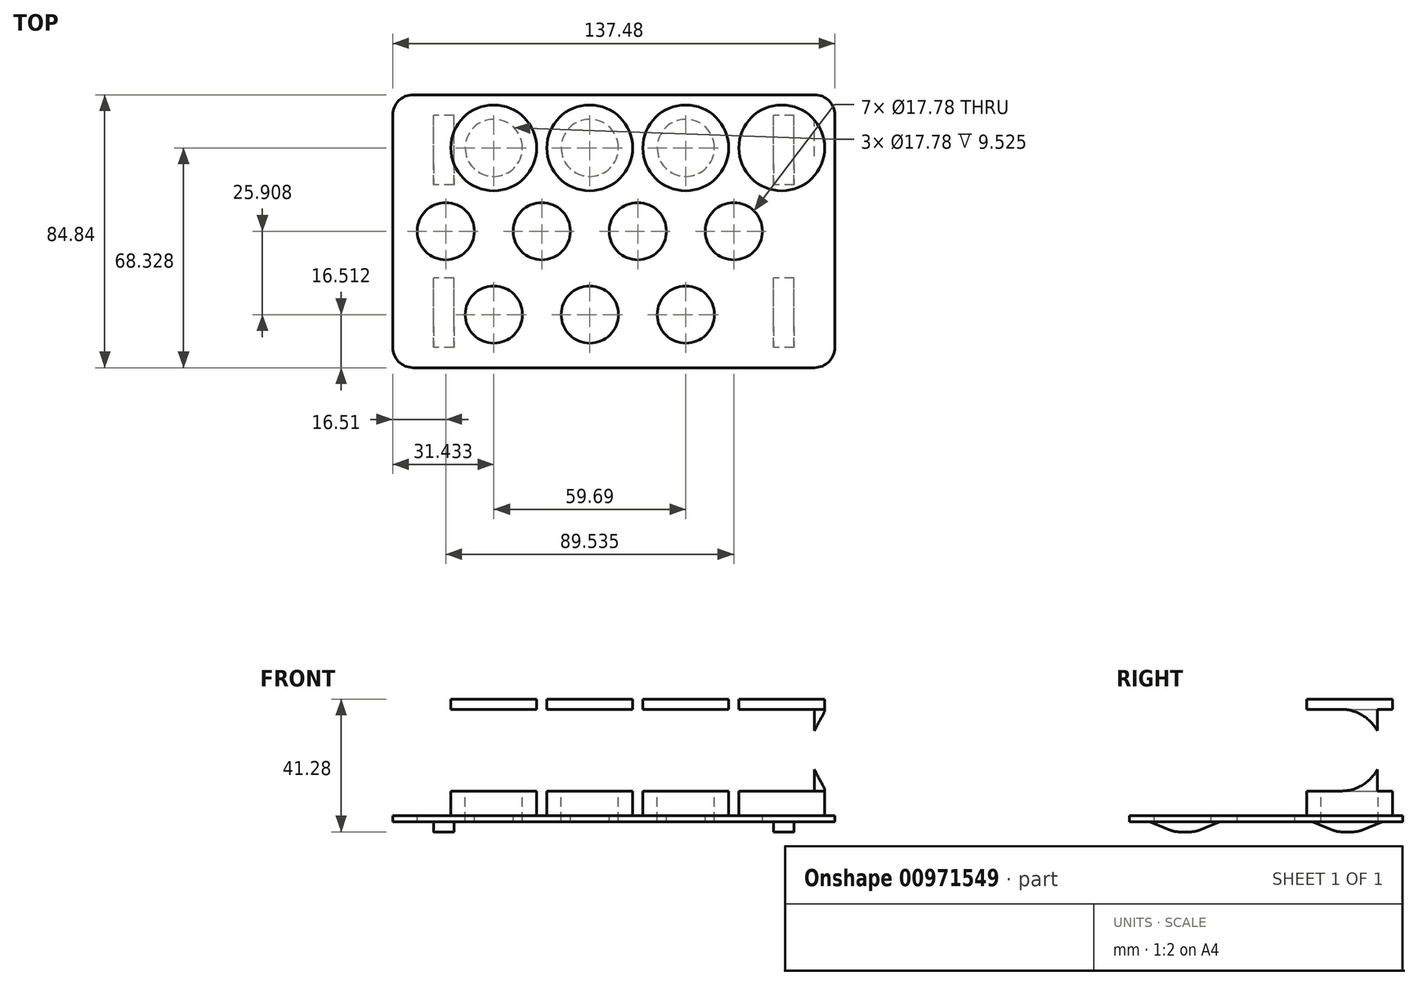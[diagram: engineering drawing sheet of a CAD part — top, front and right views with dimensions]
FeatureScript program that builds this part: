
annotation { "Feature Type Name" : "Feature", "Feature Type Description" : "" }
export const myFeature = defineFeature(function(context is Context, id is Id, definition is map)
    precondition{}
    {
        {
            var Q0;
            Q0=qCreatedBy(makeId("Right.planeOp"),FACE);
            var sketch = newSketch(context, id + "F0", { "sketchPlane" : qUnion([Q0])});
            skLineSegment(sketch, "E0.left", {"start": v(42.42, 20.64) * mm, "end": v(42.42, -17.46) * mm});
            skLineSegment(sketch, "E0.right", {"start": v(-42.42, 20.64) * mm, "end": v(-42.42, -17.46) * mm});
            skLineSegment(sketch, "E1", {"start": v(-42.42, 20.64) * mm, "end": v(42.42, 20.64) * mm});
            skLineSegment(sketch, "E2", {"start": v(28.45, -20.64) * mm, "end": v(22.1, -20.64) * mm});
            skLineSegment(sketch, "E3.top", {"start": v(42.42, -17.46) * mm, "end": v(36.07, -17.46) * mm});
            skLineSegment(sketch, "E4.top", {"start": v(-42.42, -17.46) * mm, "end": v(-36.07, -17.46) * mm});
            skLineSegment(sketch, "E5.top", {"start": v(14.48, -17.46) * mm, "end": v(-14.48, -17.46) * mm});
            skLineSegment(sketch, "E6.trimOffspring", {"start": v(-22.1, -20.64) * mm, "end": v(-28.45, -20.64) * mm});
            skLineSegment(sketch, "E7.bottom", {"start": v(23.37, 17.46) * mm, "end": v(-23.37, 17.46) * mm});
            skLineSegment(sketch, "E7.top", {"start": v(23.37, -7.94) * mm, "end": v(-23.37, -7.94) * mm});
            skLineSegment(sketch, "E7.left", {"start": v(36.07, 4.76) * mm, "end": v(36.07, 4.76) * mm});
            skLineSegment(sketch, "E7.right", {"start": v(-36.07, 4.76) * mm, "end": v(-36.07, 4.76) * mm});
            skPoint(sketch, "E8.visualSharp", {"position": v(36.07, 17.46) * mm});
            skArc(sketch, "E8.filletArc", {"start": v(36.07, 4.76) * mm, "mid": v(32.35, 13.74) * mm, "end": v(23.37, 17.46) * mm});
            skPoint(sketch, "E9.visualSharp", {"position": v(36.07, -7.94) * mm});
            skArc(sketch, "E9.filletArc", {"start": v(23.37, -7.94) * mm, "mid": v(32.35, -4.22) * mm, "end": v(36.07, 4.76) * mm});
            skPoint(sketch, "E10.visualSharp", {"position": v(-36.07, 17.46) * mm});
            skArc(sketch, "E10.filletArc", {"start": v(-23.37, 17.46) * mm, "mid": v(-32.35, 13.74) * mm, "end": v(-36.07, 4.76) * mm});
            skPoint(sketch, "E11.visualSharp", {"position": v(-36.07, -7.94) * mm});
            skArc(sketch, "E11.filletArc", {"start": v(-36.07, 4.76) * mm, "mid": v(-32.35, -4.22) * mm, "end": v(-23.37, -7.94) * mm});
            skLineSegment(sketch, "E12", {"start": v(-28.45, -20.64) * mm, "end": v(-36.07, -17.46) * mm});
            skLineSegment(sketch, "E13", {"start": v(-22.1, -20.64) * mm, "end": v(-14.48, -17.46) * mm});
            skLineSegment(sketch, "E14", {"start": v(22.1, -20.64) * mm, "end": v(14.48, -17.46) * mm});
            skLineSegment(sketch, "E15", {"start": v(28.45, -20.64) * mm, "end": v(36.07, -17.46) * mm});
            skSolve(sketch);
        }
        {
            var Q0;
            {var subQ0=sQuery(id+"F0.wireOp",EDGE,"E0.left");Q0=makeQuery(id+"F0.imprint","IMPRINT",FACE,{"disambiguationData":[TD([[makeQuery(id+"F0.imprint","IMPRINT",EDGE,{"derivedFrom":subQ0}),-1.0]])]});}
            extrude(context, id + "F1", {"entities" : qUnion([Q0]), "depth" : 137.48 * mm, "offsetDistance" : 25.4 * mm});
        }
        {
            var Q0;
            Q0=makeQuery(id+"F1.opExtrude","SWEPT_FACE",FACE,{"disambiguationData":[OSD([sQuery(id+"F0.wireOp",EDGE,"E0.left")])]});
            var sketch = newSketch(context, id + "F2", { "sketchPlane" : qUnion([Q0])});
            skLineSegment(sketch, "E16.bottom", {"start": v(-131.13, 17.46) * mm, "end": v(-6.35, 17.46) * mm});
            skLineSegment(sketch, "E16.top", {"start": v(-131.13, -7.94) * mm, "end": v(-6.35, -7.94) * mm});
            skLineSegment(sketch, "E16.left", {"start": v(-131.13, 17.46) * mm, "end": v(-131.13, -7.94) * mm});
            skLineSegment(sketch, "E16.right", {"start": v(-6.35, 17.46) * mm, "end": v(-6.35, -7.94) * mm});
            skLineSegment(sketch, "E17.bottom", {"start": v(-118.43, -17.46) * mm, "end": v(-19.05, -17.46) * mm});
            skLineSegment(sketch, "E17.top", {"start": v(-118.43, -20.64) * mm, "end": v(-19.05, -20.64) * mm});
            skLineSegment(sketch, "E17.left", {"start": v(-118.43, -17.46) * mm, "end": v(-118.43, -20.64) * mm});
            skLineSegment(sketch, "E17.right", {"start": v(-19.05, -17.46) * mm, "end": v(-19.05, -20.64) * mm});
            skLineSegment(sketch, "E18.bottom", {"start": v(-137.48, -17.46) * mm, "end": v(-124.78, -17.46) * mm});
            skLineSegment(sketch, "E18.top", {"start": v(-137.48, -20.64) * mm, "end": v(-124.78, -20.64) * mm});
            skLineSegment(sketch, "E18.left", {"start": v(-137.48, -17.46) * mm, "end": v(-137.48, -20.64) * mm});
            skLineSegment(sketch, "E18.right", {"start": v(-124.78, -17.46) * mm, "end": v(-124.78, -20.64) * mm});
            skLineSegment(sketch, "E19.bottom", {"start": v(0, -17.46) * mm, "end": v(-12.7, -17.46) * mm});
            skLineSegment(sketch, "E19.top", {"start": v(0, -20.64) * mm, "end": v(-12.7, -20.64) * mm});
            skLineSegment(sketch, "E19.left", {"start": v(0, -17.46) * mm, "end": v(0, -20.64) * mm});
            skLineSegment(sketch, "E19.right", {"start": v(-12.7, -17.46) * mm, "end": v(-12.7, -20.64) * mm});
            skSolve(sketch);
        }
        {
            var Q0;
            Q0=makeQuery(id+"F2.imprint","IMPRINT",FACE,{"disambiguationData":[TD([[makeQuery(id+"F2.imprint","IMPRINT",EDGE,{"derivedFrom":sQuery(id+"F2.wireOp",EDGE,"E16.bottom")}),-1.0]])]});
            var Q1;
            Q1=makeQuery(id+"F2.imprint","IMPRINT",FACE,{"disambiguationData":[TD([[makeQuery(id+"F2.imprint","IMPRINT",EDGE,{"derivedFrom":sQuery(id+"F2.wireOp",EDGE,"E18.bottom")}),-1.0]])]});
            var Q2;
            Q2=makeQuery(id+"F2.imprint","IMPRINT",FACE,{"disambiguationData":[TD([[makeQuery(id+"F2.imprint","IMPRINT",EDGE,{"derivedFrom":sQuery(id+"F2.wireOp",EDGE,"E17.bottom")}),-1.0]])]});
            var Q3;
            Q3=makeQuery(id+"F2.imprint","IMPRINT",FACE,{"disambiguationData":[TD([[makeQuery(id+"F2.imprint","IMPRINT",EDGE,{"derivedFrom":sQuery(id+"F2.wireOp",EDGE,"E19.bottom")}),-1.0]])]});
            extrude(context, id + "F3", {"entities" : qUnion([Q0, Q1, Q2, Q3]), "operationType" : NewBodyOperationType.REMOVE, "endBound" : BoundingType.THROUGH_ALL, "oppositeDirection" : true, "depth" : 25.4 * mm, "offsetDistance" : 25.4 * mm});
        }
        {
            var Q0;
            Q0=makeQuery(id+"F1.opExtrude","SWEPT_FACE",FACE,{"disambiguationData":[OSD([sQuery(id+"F0.wireOp",EDGE,"E1")])]});
            var sketch = newSketch(context, id + "F4", { "sketchPlane" : qUnion([Q0])});
            skCircle(sketch, "E20", {"center": v(16.51, 0) * mm, "radius": 13.34 * mm});
            skCircle(sketch, "E21", {"center": v(46.36, 0) * mm, "radius": 13.34 * mm});
            skCircle(sketch, "E22", {"center": v(76.2, 0) * mm, "radius": 13.34 * mm});
            skCircle(sketch, "E23", {"center": v(106.05, 0) * mm, "radius": 13.34 * mm});
            skCircle(sketch, "E24", {"center": v(31.43, -25.9) * mm, "radius": 13.34 * mm});
            skCircle(sketch, "E25.MirrorC", {"center": v(31.43, 25.9) * mm, "radius": 13.34 * mm});
            skCircle(sketch, "E26", {"center": v(61.28, -25.9) * mm, "radius": 13.34 * mm});
            skCircle(sketch, "E27", {"center": v(91.12, -25.9) * mm, "radius": 13.34 * mm});
            skCircle(sketch, "E28", {"center": v(120.97, -25.9) * mm, "radius": 13.34 * mm});
            skCircle(sketch, "E29.MirrorC", {"center": v(61.28, 25.9) * mm, "radius": 13.34 * mm});
            skCircle(sketch, "E30.MirrorC", {"center": v(91.12, 25.9) * mm, "radius": 13.34 * mm});
            skCircle(sketch, "E31.MirrorC", {"center": v(120.97, 25.9) * mm, "radius": 13.34 * mm});
            skLineSegment(sketch, "E32.bottom", {"start": v(128.43, 10.67) * mm, "end": v(128.43, 10.67) * mm});
            skLineSegment(sketch, "E32.top", {"start": v(128.43, -10.67) * mm, "end": v(128.43, -10.67) * mm});
            skLineSegment(sketch, "E32.left", {"start": v(134.3, 4.8) * mm, "end": v(134.3, -4.8) * mm});
            skLineSegment(sketch, "E32.right", {"start": v(122.56, 4.8) * mm, "end": v(122.56, -4.8) * mm});
            skPoint(sketch, "E32.middle", {"position": v(128.43, 0) * mm});
            skPoint(sketch, "E33.visualSharp", {"position": v(134.3, -10.67) * mm});
            skArc(sketch, "E33.filletArc", {"start": v(128.43, -10.67) * mm, "mid": v(132.58, -8.95) * mm, "end": v(134.3, -4.8) * mm});
            skPoint(sketch, "E34.visualSharp", {"position": v(122.56, -10.67) * mm});
            skArc(sketch, "E34.filletArc", {"start": v(122.56, -4.8) * mm, "mid": v(124.28, -8.95) * mm, "end": v(128.43, -10.67) * mm});
            skPoint(sketch, "E35.visualSharp", {"position": v(122.56, 10.67) * mm});
            skArc(sketch, "E35.filletArc", {"start": v(128.43, 10.67) * mm, "mid": v(124.28, 8.95) * mm, "end": v(122.56, 4.8) * mm});
            skPoint(sketch, "E36.visualSharp", {"position": v(134.3, 10.67) * mm});
            skArc(sketch, "E36.filletArc", {"start": v(134.3, 4.8) * mm, "mid": v(132.58, 8.95) * mm, "end": v(128.43, 10.67) * mm});
            skLineSegment(sketch, "E37.bottom", {"start": v(9.05, -16.51) * mm, "end": v(9.05, -16.51) * mm});
            skLineSegment(sketch, "E37.top", {"start": v(9.05, -39.24) * mm, "end": v(9.05, -39.24) * mm});
            skLineSegment(sketch, "E37.left", {"start": v(3.17, -22.38) * mm, "end": v(3.18, -33.37) * mm});
            skLineSegment(sketch, "E37.right", {"start": v(14.92, -22.38) * mm, "end": v(14.92, -33.37) * mm});
            skPoint(sketch, "E37.middle", {"position": v(9.05, -27.88) * mm});
            skPoint(sketch, "E38.visualSharp", {"position": v(14.92, -39.24) * mm});
            skArc(sketch, "E38.filletArc", {"start": v(9.05, -39.24) * mm, "mid": v(13.2, -37.52) * mm, "end": v(14.92, -33.37) * mm});
            skPoint(sketch, "E39.visualSharp", {"position": v(3.18, -39.24) * mm});
            skArc(sketch, "E39.filletArc", {"start": v(3.18, -33.37) * mm, "mid": v(4.9, -37.52) * mm, "end": v(9.05, -39.24) * mm});
            skPoint(sketch, "E40.visualSharp", {"position": v(14.92, -16.5) * mm});
            skArc(sketch, "E40.filletArc", {"start": v(14.92, -22.38) * mm, "mid": v(13.2, -18.23) * mm, "end": v(9.05, -16.51) * mm});
            skPoint(sketch, "E41.visualSharp", {"position": v(3.17, -16.51) * mm});
            skArc(sketch, "E41.filletArc", {"start": v(9.05, -16.51) * mm, "mid": v(4.9, -18.23) * mm, "end": v(3.18, -22.38) * mm});
            skLineSegment(sketch, "E42.MirrorCS", {"start": v(14.92, 22.38) * mm, "end": v(14.92, 33.37) * mm});
            skArc(sketch, "E43.MirrorCS", {"start": v(9.05, 39.24) * mm, "mid": v(13.2, 37.52) * mm, "end": v(14.92, 33.37) * mm});
            skArc(sketch, "E44.MirrorCS", {"start": v(3.18, 33.37) * mm, "mid": v(4.9, 37.52) * mm, "end": v(9.05, 39.24) * mm});
            skLineSegment(sketch, "E45.MirrorCS", {"start": v(3.17, 22.38) * mm, "end": v(3.18, 33.37) * mm});
            skArc(sketch, "E46.MirrorCS", {"start": v(9.05, 16.51) * mm, "mid": v(4.9, 18.23) * mm, "end": v(3.18, 22.38) * mm});
            skArc(sketch, "E47.MirrorCS", {"start": v(14.92, 22.38) * mm, "mid": v(13.2, 18.23) * mm, "end": v(9.05, 16.51) * mm});
            skSolve(sketch);
        }
        {
            var Q0;
            Q0=makeQuery(id+"F4.imprint","IMPRINT",FACE,{"disambiguationData":[TD([[makeQuery(id+"F4.imprint","IMPRINT",EDGE,{"derivedFrom":sQuery(id+"F4.wireOp",EDGE,"jm78994w-IAon-zNqe-jNT5-EaWAa206wX2G")}),1.0]])]});
            var Q1;
            Q1=makeQuery(id+"F4.imprint","IMPRINT",FACE,{"disambiguationData":[TD([[makeQuery(id+"F4.imprint","IMPRINT",EDGE,{"derivedFrom":sQuery(id+"F4.wireOp",EDGE,"Kh83bSks-6wL4-LwiD-ftK5-UFU7rUHDjcQT")}),1.0]])]});
            var Q2;
            Q2=makeQuery(id+"F4.imprint","IMPRINT",FACE,{"disambiguationData":[TD([[makeQuery(id+"F4.imprint","IMPRINT",EDGE,{"derivedFrom":sQuery(id+"F4.wireOp",EDGE,"tLHcckMa-RLEo-CRu1-Yicz-MQPrtSImhYbt")}),1.0]])]});
            var Q3;
            Q3=makeQuery(id+"F4.imprint","IMPRINT",FACE,{"disambiguationData":[TD([[makeQuery(id+"F4.imprint","IMPRINT",EDGE,{"derivedFrom":sQuery(id+"F4.wireOp",EDGE,"o5KPIwwS-8ylI-uTK5-LI3t-9iqvxFOEiAom")}),1.0]])]});
            var Q4;
            Q4=makeQuery(id+"F4.imprint","IMPRINT",FACE,{"disambiguationData":[TD([[makeQuery(id+"F4.imprint","IMPRINT",EDGE,{"derivedFrom":sQuery(id+"F4.wireOp",EDGE,"AhIFXKle-6ren-T3tb-L6Av-1iPCFqoMsREZ")}),1.0]])]});
            var Q5;
            Q5=makeQuery(id+"F4.imprint","IMPRINT",FACE,{"disambiguationData":[TD([[makeQuery(id+"F4.imprint","IMPRINT",EDGE,{"derivedFrom":sQuery(id+"F4.wireOp",EDGE,"wPVB1F3V-20fs-MMbR-FTxM-zm3m0jVc7lvQ")}),1.0]])]});
            var Q6;
            Q6=makeQuery(id+"F4.imprint","IMPRINT",FACE,{"disambiguationData":[TD([[makeQuery(id+"F4.imprint","IMPRINT",EDGE,{"derivedFrom":sQuery(id+"F4.wireOp",EDGE,"T3ZcG9Cn-MawP-cxRy-pQcX-JEefpN5sOvam")}),1.0]])]});
            var Q7;
            Q7=makeQuery(id+"F4.imprint","IMPRINT",FACE,{"disambiguationData":[TD([[makeQuery(id+"F4.imprint","IMPRINT",EDGE,{"derivedFrom":sQuery(id+"F4.wireOp",EDGE,"XZ3QAXgJ-CkEy-Kyhc-Jaey-V5kokyXw6pyG")}),1.0]])]});
            var Q8;
            Q8=makeQuery(id+"F4.imprint","IMPRINT",FACE,{"disambiguationData":[TD([[makeQuery(id+"F4.imprint","IMPRINT",EDGE,{"derivedFrom":sQuery(id+"F4.wireOp",EDGE,"E20")}),1.0]])]});
            var Q9;
            Q9=makeQuery(id+"F4.imprint","IMPRINT",FACE,{"disambiguationData":[TD([[makeQuery(id+"F4.imprint","IMPRINT",EDGE,{"derivedFrom":sQuery(id+"F4.wireOp",EDGE,"E21")}),1.0]])]});
            var Q10;
            Q10=makeQuery(id+"F4.imprint","IMPRINT",FACE,{"disambiguationData":[TD([[makeQuery(id+"F4.imprint","IMPRINT",EDGE,{"derivedFrom":sQuery(id+"F4.wireOp",EDGE,"E22")}),1.0]])]});
            var Q11;
            Q11=makeQuery(id+"F4.imprint","IMPRINT",FACE,{"disambiguationData":[TD([[makeQuery(id+"F4.imprint","IMPRINT",EDGE,{"derivedFrom":sQuery(id+"F4.wireOp",EDGE,"E23")}),1.0]])]});
            var Q12;
            Q12=makeQuery(id+"F4.imprint","IMPRINT",FACE,{"disambiguationData":[TD([[makeQuery(id+"F4.imprint","IMPRINT",EDGE,{"derivedFrom":sQuery(id+"F4.wireOp",EDGE,"vciMU1Vq-kYBW-qjiw-Wg2y-pd83fXojDvpy.bottom")}),-1.0]])]});
            var Q13;
            Q13=makeQuery(id+"F4.imprint","IMPRINT",FACE,{"disambiguationData":[TD([[makeQuery(id+"F4.imprint","IMPRINT",EDGE,{"derivedFrom":sQuery(id+"F4.wireOp",EDGE,"da6486c7-8e97-4326-bfba-02a94056a75e0.MirrorC")}),-1.0]])]});
            var Q14;
            Q14=makeQuery(id+"F4.imprint","IMPRINT",FACE,{"disambiguationData":[TD([[makeQuery(id+"F4.imprint","IMPRINT",EDGE,{"derivedFrom":sQuery(id+"F4.wireOp",EDGE,"d492e33b-482a-4f5a-a7fa-c0e94ef1090a0.MirrorC")}),-1.0]])]});
            var Q15;
            Q15=makeQuery(id+"F4.imprint","IMPRINT",FACE,{"disambiguationData":[TD([[makeQuery(id+"F4.imprint","IMPRINT",EDGE,{"derivedFrom":sQuery(id+"F4.wireOp",EDGE,"0d012fd1-caaa-4a50-bc96-0bbd9ba7731a0.MirrorC")}),-1.0]])]});
            var Q16;
            Q16=makeQuery(id+"F4.imprint","IMPRINT",FACE,{"disambiguationData":[TD([[makeQuery(id+"F4.imprint","IMPRINT",EDGE,{"derivedFrom":sQuery(id+"F4.wireOp",EDGE,"06f5e0d1-2cf6-4067-87b7-a4061e7c41f80.MirrorC")}),-1.0]])]});
            var Q17;
            Q17=makeQuery(id+"F4.imprint","IMPRINT",FACE,{"disambiguationData":[TD([[makeQuery(id+"F4.imprint","IMPRINT",EDGE,{"derivedFrom":sQuery(id+"F4.wireOp",EDGE,"c6291b78-575e-4a72-a550-4777f93526100.MirrorC")}),-1.0]])]});
            var Q18;
            Q18=makeQuery(id+"F4.imprint","IMPRINT",FACE,{"disambiguationData":[TD([[makeQuery(id+"F4.imprint","IMPRINT",EDGE,{"derivedFrom":sQuery(id+"F4.wireOp",EDGE,"f3e2f5e7-102e-45df-8559-8a6ab0aaba5b0.MirrorC")}),-1.0]])]});
            var Q19;
            Q19=makeQuery(id+"F4.imprint","IMPRINT",FACE,{"disambiguationData":[TD([[makeQuery(id+"F4.imprint","IMPRINT",EDGE,{"derivedFrom":sQuery(id+"F4.wireOp",EDGE,"dd626ad0-a420-4f17-bbb8-cdf8eb234abf0.MirrorC")}),-1.0]])]});
            var Q20;
            Q20=makeQuery(id+"F4.imprint","IMPRINT",FACE,{"disambiguationData":[TD([[makeQuery(id+"F4.imprint","IMPRINT",EDGE,{"derivedFrom":sQuery(id+"F4.wireOp",EDGE,"f3a2bc9c-32a0-4c81-a079-4487179850330.MirrorC")}),-1.0]])]});
            var Q21;
            Q21=makeQuery(id+"F4.imprint","IMPRINT",FACE,{"disambiguationData":[TD([[makeQuery(id+"F4.imprint","IMPRINT",EDGE,{"derivedFrom":sQuery(id+"F4.wireOp",EDGE,"MwGZwXsl-6qpJ-SU0V-yodx-YUyaRHULoMgz.bottom")}),-1.0]])]});
            var Q22;
            Q22=makeQuery(id+"F4.imprint","IMPRINT",FACE,{"disambiguationData":[TD([[makeQuery(id+"F4.imprint","IMPRINT",EDGE,{"derivedFrom":sQuery(id+"F4.wireOp",EDGE,"4f9bcf4e-a4b3-4607-940e-24dab36a3d102.MirrorCS")}),-1.0]])]});
            var Q23;
            Q23=makeQuery(id+"F4.imprint","IMPRINT",FACE,{"disambiguationData":[TD([[makeQuery(id+"F4.imprint","IMPRINT",EDGE,{"derivedFrom":sQuery(id+"F4.wireOp",EDGE,"cda0069e-aa66-46fa-98c6-f49124ae65170.MirrorC")}),-1.0]])]});
            var Q24;
            Q24=makeQuery(id+"F4.imprint","IMPRINT",FACE,{"disambiguationData":[TD([[makeQuery(id+"F4.imprint","IMPRINT",EDGE,{"derivedFrom":sQuery(id+"F4.wireOp",EDGE,"634edb4d-20c6-4c1e-9da3-65a24131e6f80.MirrorC")}),-1.0]])]});
            var Q25;
            Q25=makeQuery(id+"F4.imprint","IMPRINT",FACE,{"disambiguationData":[TD([[makeQuery(id+"F4.imprint","IMPRINT",EDGE,{"derivedFrom":sQuery(id+"F4.wireOp",EDGE,"adaf3b54-f3d4-46e2-a9e6-fe95a4b0e5ad0.MirrorC")}),-1.0]])]});
            var Q26;
            Q26=makeQuery(id+"F4.imprint","IMPRINT",FACE,{"disambiguationData":[TD([[makeQuery(id+"F4.imprint","IMPRINT",EDGE,{"derivedFrom":sQuery(id+"F4.wireOp",EDGE,"7d7bd67a-6d43-402b-96e0-67d232c9219e0.MirrorC")}),-1.0]])]});
            var Q27;
            Q27=makeQuery(id+"F4.imprint","IMPRINT",FACE,{"disambiguationData":[TD([[makeQuery(id+"F4.imprint","IMPRINT",EDGE,{"derivedFrom":sQuery(id+"F4.wireOp",EDGE,"0194b1ae-9eff-4578-bf86-ca53363185000.MirrorC")}),-1.0]])]});
            var Q28;
            Q28=makeQuery(id+"F4.imprint","IMPRINT",FACE,{"disambiguationData":[TD([[makeQuery(id+"F4.imprint","IMPRINT",EDGE,{"derivedFrom":sQuery(id+"F4.wireOp",EDGE,"ae09e1ef-a855-4ca2-9e50-b030dd3f02470.MirrorC")}),-1.0]])]});
            var Q29;
            Q29=makeQuery(id+"F4.imprint","IMPRINT",FACE,{"disambiguationData":[TD([[makeQuery(id+"F4.imprint","IMPRINT",EDGE,{"derivedFrom":sQuery(id+"F4.wireOp",EDGE,"oiPZrtKw-9CO2-Gcmp-UDcG-Zl46WvTLTXzR")}),1.0]])]});
            var Q30;
            Q30=makeQuery(id+"F4.imprint","IMPRINT",FACE,{"disambiguationData":[TD([[makeQuery(id+"F4.imprint","IMPRINT",EDGE,{"derivedFrom":sQuery(id+"F4.wireOp",EDGE,"WJXtel3u-SdeV-AbK0-67Dp-bjXxcufvXJ9Y")}),1.0]])]});
            var Q31;
            Q31=makeQuery(id+"F4.imprint","IMPRINT",FACE,{"disambiguationData":[TD([[makeQuery(id+"F4.imprint","IMPRINT",EDGE,{"derivedFrom":sQuery(id+"F4.wireOp",EDGE,"hWOCtbjO-zSSX-Dv2g-DN5h-ATAyDXn6fbtZ")}),1.0]])]});
            var Q32;
            Q32=makeQuery(id+"F4.imprint","IMPRINT",FACE,{"disambiguationData":[TD([[makeQuery(id+"F4.imprint","IMPRINT",EDGE,{"derivedFrom":sQuery(id+"F4.wireOp",EDGE,"ZuNiJv4I-s0Zy-MzRI-5lCJ-zCoPcHUsg3ar")}),1.0]])]});
            var Q33;
            Q33=makeQuery(id+"F4.imprint","IMPRINT",FACE,{"disambiguationData":[TD([[makeQuery(id+"F4.imprint","IMPRINT",EDGE,{"derivedFrom":sQuery(id+"F4.wireOp",EDGE,"tNnFtRH8-iYHT-WWZi-w1Vm-MyPOb0I7dEfi")}),1.0]])]});
            var Q34;
            Q34=makeQuery(id+"F4.imprint","IMPRINT",FACE,{"disambiguationData":[TD([[makeQuery(id+"F4.imprint","IMPRINT",EDGE,{"derivedFrom":sQuery(id+"F4.wireOp",EDGE,"HWqQpDHg-kzO7-goh1-WeDl-2Kc1Ie6DcMvE")}),1.0]])]});
            var Q35;
            Q35=makeQuery(id+"F4.imprint","IMPRINT",FACE,{"disambiguationData":[TD([[makeQuery(id+"F4.imprint","IMPRINT",EDGE,{"derivedFrom":sQuery(id+"F4.wireOp",EDGE,"MwGZwXsl-6qpJ-SU0V-yodx-YUyaRHULoMgz.left")}),1.0]])]});
            var Q36;
            Q36=makeQuery(id+"F4.imprint","IMPRINT",FACE,{"disambiguationData":[TD([[makeQuery(id+"F4.imprint","IMPRINT",EDGE,{"derivedFrom":sQuery(id+"F4.wireOp",EDGE,"vciMU1Vq-kYBW-qjiw-Wg2y-pd83fXojDvpy.left")}),1.0]])]});
            var Q37;
            Q37=makeQuery(id+"F4.imprint","IMPRINT",FACE,{"disambiguationData":[TD([[makeQuery(id+"F4.imprint","IMPRINT",EDGE,{"derivedFrom":sQuery(id+"F4.wireOp",EDGE,"E28")}),1.0]])]});
            var Q38;
            Q38=makeQuery(id+"F4.imprint","IMPRINT",FACE,{"disambiguationData":[TD([[makeQuery(id+"F4.imprint","IMPRINT",EDGE,{"derivedFrom":sQuery(id+"F4.wireOp",EDGE,"E27")}),1.0]])]});
            var Q39;
            Q39=makeQuery(id+"F4.imprint","IMPRINT",FACE,{"disambiguationData":[TD([[makeQuery(id+"F4.imprint","IMPRINT",EDGE,{"derivedFrom":sQuery(id+"F4.wireOp",EDGE,"E26")}),1.0]])]});
            var Q40;
            Q40=makeQuery(id+"F4.imprint","IMPRINT",FACE,{"disambiguationData":[TD([[makeQuery(id+"F4.imprint","IMPRINT",EDGE,{"derivedFrom":sQuery(id+"F4.wireOp",EDGE,"E24")}),1.0]])]});
            var Q41;
            Q41=makeQuery(id+"F4.imprint","IMPRINT",FACE,{"disambiguationData":[TD([[makeQuery(id+"F4.imprint","IMPRINT",EDGE,{"derivedFrom":sQuery(id+"F4.wireOp",EDGE,"E25.MirrorC")}),-1.0]])]});
            var Q42;
            Q42=makeQuery(id+"F4.imprint","IMPRINT",FACE,{"disambiguationData":[TD([[makeQuery(id+"F4.imprint","IMPRINT",EDGE,{"derivedFrom":sQuery(id+"F4.wireOp",EDGE,"E29.MirrorC")}),-1.0]])]});
            var Q43;
            Q43=makeQuery(id+"F4.imprint","IMPRINT",FACE,{"disambiguationData":[TD([[makeQuery(id+"F4.imprint","IMPRINT",EDGE,{"derivedFrom":sQuery(id+"F4.wireOp",EDGE,"E30.MirrorC")}),-1.0]])]});
            var Q44;
            Q44=makeQuery(id+"F4.imprint","IMPRINT",FACE,{"disambiguationData":[TD([[makeQuery(id+"F4.imprint","IMPRINT",EDGE,{"derivedFrom":sQuery(id+"F4.wireOp",EDGE,"E31.MirrorC")}),-1.0]])]});
            var Q45;
            Q45=makeQuery(id+"F4.imprint","IMPRINT",FACE,{"disambiguationData":[TD([[makeQuery(id+"F4.imprint","IMPRINT",EDGE,{"derivedFrom":sQuery(id+"F4.wireOp",EDGE,"E37.left")}),1.0]])]});
            var Q46;
            Q46=makeQuery(id+"F4.imprint","IMPRINT",FACE,{"disambiguationData":[TD([[makeQuery(id+"F4.imprint","IMPRINT",EDGE,{"derivedFrom":sQuery(id+"F4.wireOp",EDGE,"E42.MirrorCS")}),1.0]])]});
            var Q47;
            Q47=makeQuery(id+"F4.imprint","IMPRINT",FACE,{"disambiguationData":[TD([[makeQuery(id+"F4.imprint","IMPRINT",EDGE,{"derivedFrom":sQuery(id+"F4.wireOp",EDGE,"E32.left")}),-1.0]])]});
            extrude(context, id + "F5", {"entities" : qUnion([Q0, Q1, Q2, Q3, Q4, Q5, Q6, Q7, Q8, Q9, Q10, Q11, Q12, Q13, Q14, Q15, Q16, Q17, Q18, Q19, Q20, Q21, Q22, Q23, Q24, Q25, Q26, Q27, Q28, Q29, Q30, Q31, Q32, Q33, Q34, Q35, Q36, Q37, Q38, Q39, Q40, Q41, Q42, Q43, Q44, Q45, Q46, Q47]), "operationType" : NewBodyOperationType.REMOVE, "oppositeDirection" : true, "depth" : 36.2 * mm, "offsetDistance" : 25.4 * mm});
        }
        {
            var Q0;
            Q0=makeQuery(id+"F1.opExtrude","CAP_EDGE",EDGE,{"disambiguationData":[OSD([sQuery(id+"F0.wireOp",EDGE,"E0.left")])],"isStart":true});
            var Q1;
            Q1=makeQuery(id+"F1.opExtrude","CAP_EDGE",EDGE,{"disambiguationData":[OSD([sQuery(id+"F0.wireOp",EDGE,"E0.right")])],"isStart":true});
            var Q2;
            Q2=makeQuery(id+"F1.opExtrude","CAP_EDGE",EDGE,{"disambiguationData":[OSD([sQuery(id+"F0.wireOp",EDGE,"E0.right")])],"isStart":false});
            var Q3;
            Q3=makeQuery(id+"F1.opExtrude","CAP_EDGE",EDGE,{"disambiguationData":[OSD([sQuery(id+"F0.wireOp",EDGE,"E0.left")])],"isStart":false});
            fillet(context, id + "F6", {"entities" : qUnion([Q0, Q1, Q2, Q3]), "radius" : 6.35 * mm, "tangentPropagation" : true, "allowEdgeOverflow" : false});
        }
        {
            var Q0;
            Q0=makeQuery(id+"F3.boolean.opBoolean","MERGE",FACE,{"derivedFrom":[makeQuery(id+"F1.opExtrude","SWEPT_FACE",FACE,{"disambiguationData":[OSD([sQuery(id+"F0.wireOp",EDGE,"E3.top")])]}),makeQuery(id+"F1.opExtrude","SWEPT_FACE",FACE,{"disambiguationData":[OSD([sQuery(id+"F0.wireOp",EDGE,"E4.top")])]}),makeQuery(id+"F1.opExtrude","SWEPT_FACE",FACE,{"disambiguationData":[OSD([sQuery(id+"F0.wireOp",EDGE,"E5.top")])]})],"fromTools":[makeQuery(id+"F3.opExtrude","SWEPT_FACE",FACE,{"disambiguationData":[OSD([sQuery(id+"F2.wireOp",EDGE,"E17.bottom")])]}),makeQuery(id+"F3.opExtrude","SWEPT_FACE",FACE,{"disambiguationData":[OSD([sQuery(id+"F2.wireOp",EDGE,"E18.bottom")])]}),makeQuery(id+"F3.opExtrude","SWEPT_FACE",FACE,{"disambiguationData":[OSD([sQuery(id+"F2.wireOp",EDGE,"E19.bottom")])]})]});
            var sketch = newSketch(context, id + "F7", { "sketchPlane" : qUnion([Q0])});
            skCircle(sketch, "E48", {"center": v(16.51, 0) * mm, "radius": 8.9 * mm});
            skCircle(sketch, "E49", {"center": v(46.36, 0) * mm, "radius": 8.9 * mm});
            skCircle(sketch, "E50", {"center": v(76.2, 0) * mm, "radius": 8.9 * mm});
            skCircle(sketch, "E51", {"center": v(106.05, 0) * mm, "radius": 8.9 * mm});
            skCircle(sketch, "E52", {"center": v(31.43, 25.9) * mm, "radius": 8.9 * mm});
            skCircle(sketch, "E53", {"center": v(61.28, 25.9) * mm, "radius": 8.9 * mm});
            skCircle(sketch, "E54", {"center": v(91.12, 25.9) * mm, "radius": 8.9 * mm});
            skCircle(sketch, "E55.MirrorC", {"center": v(91.12, -25.9) * mm, "radius": 8.9 * mm});
            skCircle(sketch, "E56.MirrorC", {"center": v(61.28, -25.9) * mm, "radius": 8.9 * mm});
            skCircle(sketch, "E57.MirrorC", {"center": v(31.43, -25.9) * mm, "radius": 8.9 * mm});
            skSolve(sketch);
        }
        {
            var Q0;
            Q0 = qSketchRegion(id + "F7", true);
            extrude(context, id + "F8", {"entities" : qUnion([Q0]), "operationType" : NewBodyOperationType.REMOVE, "endBound" : BoundingType.SYMMETRIC, "depth" : 25.4 * mm, "offsetDistance" : 25.4 * mm});
        }
        {
            var Q0;
            {var subQ0=sQuery(id+"F0.wireOp",EDGE,"E2");var subQ1=sQuery(id+"F0.wireOp",EDGE,"E15");Q0=makeQuery(id+"F3.boolean.opBoolean","SPLIT",EDGE,{"disambiguationData":[TD([makeQuery(id+"F3.opExtrude","SWEPT_FACE",FACE,{"disambiguationData":[OSD([sQuery(id+"F2.wireOp",EDGE,"E17.left")])]})])],"derivedFrom":makeQuery(id+"F1.opExtrude","SWEPT_EDGE",EDGE,{"disambiguationData":[OSD([subQ0,subQ1])]})});}
            var Q1;
            {var subQ0=sQuery(id+"F0.wireOp",EDGE,"E2");var subQ1=sQuery(id+"F0.wireOp",EDGE,"E14");Q1=makeQuery(id+"F3.boolean.opBoolean","SPLIT",EDGE,{"disambiguationData":[TD([makeQuery(id+"F3.opExtrude","SWEPT_FACE",FACE,{"disambiguationData":[OSD([sQuery(id+"F2.wireOp",EDGE,"E17.left")])]})])],"derivedFrom":makeQuery(id+"F1.opExtrude","SWEPT_EDGE",EDGE,{"disambiguationData":[OSD([subQ0,subQ1])]})});}
            var Q2;
            {var subQ0=sQuery(id+"F0.wireOp",EDGE,"E6.trimOffspring");var subQ1=sQuery(id+"F0.wireOp",EDGE,"E13");Q2=makeQuery(id+"F3.boolean.opBoolean","SPLIT",EDGE,{"disambiguationData":[TD([makeQuery(id+"F3.opExtrude","SWEPT_FACE",FACE,{"disambiguationData":[OSD([sQuery(id+"F2.wireOp",EDGE,"E17.left")])]})])],"derivedFrom":makeQuery(id+"F1.opExtrude","SWEPT_EDGE",EDGE,{"disambiguationData":[OSD([subQ0,subQ1])]})});}
            var Q3;
            {var subQ0=sQuery(id+"F0.wireOp",EDGE,"E6.trimOffspring");var subQ1=sQuery(id+"F0.wireOp",EDGE,"E12");Q3=makeQuery(id+"F3.boolean.opBoolean","SPLIT",EDGE,{"disambiguationData":[TD([makeQuery(id+"F3.opExtrude","SWEPT_FACE",FACE,{"disambiguationData":[OSD([sQuery(id+"F2.wireOp",EDGE,"E17.left")])]})])],"derivedFrom":makeQuery(id+"F1.opExtrude","SWEPT_EDGE",EDGE,{"disambiguationData":[OSD([subQ0,subQ1])]})});}
            var Q4;
            {var subQ0=sQuery(id+"F0.wireOp",EDGE,"E2");var subQ1=sQuery(id+"F0.wireOp",EDGE,"E15");Q4=makeQuery(id+"F3.boolean.opBoolean","SPLIT",EDGE,{"disambiguationData":[TD([makeQuery(id+"F3.opExtrude","SWEPT_FACE",FACE,{"disambiguationData":[OSD([sQuery(id+"F2.wireOp",EDGE,"E17.right")])]})])],"derivedFrom":makeQuery(id+"F1.opExtrude","SWEPT_EDGE",EDGE,{"disambiguationData":[OSD([subQ0,subQ1])]})});}
            var Q5;
            {var subQ0=sQuery(id+"F0.wireOp",EDGE,"E2");var subQ1=sQuery(id+"F0.wireOp",EDGE,"E14");Q5=makeQuery(id+"F3.boolean.opBoolean","SPLIT",EDGE,{"disambiguationData":[TD([makeQuery(id+"F3.opExtrude","SWEPT_FACE",FACE,{"disambiguationData":[OSD([sQuery(id+"F2.wireOp",EDGE,"E17.right")])]})])],"derivedFrom":makeQuery(id+"F1.opExtrude","SWEPT_EDGE",EDGE,{"disambiguationData":[OSD([subQ0,subQ1])]})});}
            var Q6;
            {var subQ0=sQuery(id+"F0.wireOp",EDGE,"E6.trimOffspring");var subQ1=sQuery(id+"F0.wireOp",EDGE,"E13");Q6=makeQuery(id+"F3.boolean.opBoolean","SPLIT",EDGE,{"disambiguationData":[TD([makeQuery(id+"F3.opExtrude","SWEPT_FACE",FACE,{"disambiguationData":[OSD([sQuery(id+"F2.wireOp",EDGE,"E17.right")])]})])],"derivedFrom":makeQuery(id+"F1.opExtrude","SWEPT_EDGE",EDGE,{"disambiguationData":[OSD([subQ0,subQ1])]})});}
            var Q7;
            {var subQ0=sQuery(id+"F0.wireOp",EDGE,"E6.trimOffspring");var subQ1=sQuery(id+"F0.wireOp",EDGE,"E12");Q7=makeQuery(id+"F3.boolean.opBoolean","SPLIT",EDGE,{"disambiguationData":[TD([makeQuery(id+"F3.opExtrude","SWEPT_FACE",FACE,{"disambiguationData":[OSD([sQuery(id+"F2.wireOp",EDGE,"E17.right")])]})])],"derivedFrom":makeQuery(id+"F1.opExtrude","SWEPT_EDGE",EDGE,{"disambiguationData":[OSD([subQ0,subQ1])]})});}
            fillet(context, id + "F9", {"entities" : qUnion([Q0, Q1, Q2, Q3, Q4, Q5, Q6, Q7]), "radius" : 6.35 * mm, "tangentPropagation" : true, "allowEdgeOverflow" : false});
        }
    });
